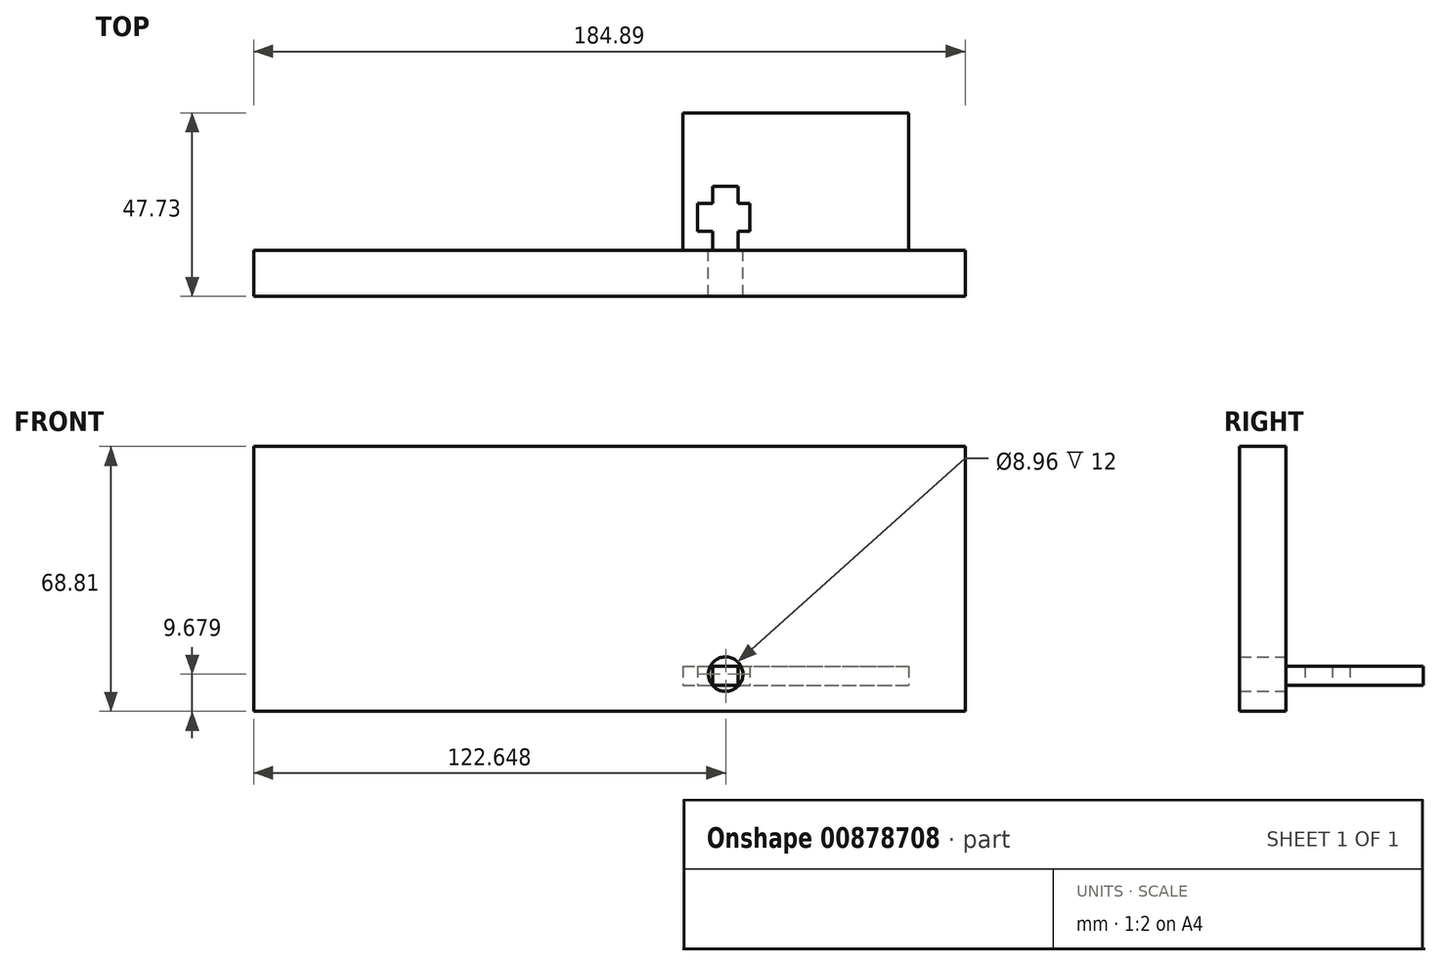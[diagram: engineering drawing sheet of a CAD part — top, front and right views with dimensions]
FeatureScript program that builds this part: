
annotation { "Feature Type Name" : "Feature", "Feature Type Description" : "" }
export const myFeature = defineFeature(function(context is Context, id is Id, definition is map)
    precondition{}
    {
        {
            var Q0;
            Q0=qCreatedBy(makeId("Top.planeOp"),FACE);
            var sketch = newSketch(context, id + "F0", { "sketchPlane" : qUnion([Q0])});
            skLineSegment(sketch, "E0.bottom", {"start": v(0, 0) * mm, "end": v(58.66, 0) * mm});
            skLineSegment(sketch, "E0.top", {"start": v(0, 35.73) * mm, "end": v(58.66, 35.73) * mm});
            skLineSegment(sketch, "E0.left", {"start": v(0, 0) * mm, "end": v(0, 35.73) * mm});
            skLineSegment(sketch, "E0.right", {"start": v(58.66, 0) * mm, "end": v(58.66, 35.73) * mm});
            skLineSegment(sketch, "E1.bottom", {"start": v(7.74, 0) * mm, "end": v(14.43, 0) * mm});
            skLineSegment(sketch, "E1.top", {"start": v(7.74, 4.95) * mm, "end": v(14.43, 4.95) * mm});
            skLineSegment(sketch, "E1.left", {"start": v(7.74, 0) * mm, "end": v(7.74, 4.95) * mm});
            skLineSegment(sketch, "E1.right", {"start": v(14.43, 0) * mm, "end": v(14.43, 4.95) * mm});
            skLineSegment(sketch, "E2.bottom", {"start": v(3.84, 4.95) * mm, "end": v(17.45, 4.95) * mm});
            skLineSegment(sketch, "E2.top", {"start": v(3.84, 12.14) * mm, "end": v(17.45, 12.14) * mm});
            skLineSegment(sketch, "E2.left", {"start": v(3.84, 4.95) * mm, "end": v(3.84, 12.14) * mm});
            skLineSegment(sketch, "E2.right", {"start": v(17.45, 4.95) * mm, "end": v(17.45, 12.14) * mm});
            skPoint(sketch, "E3.firstSnap0", {"position": v(10.65, 12.14) * mm});
            skLineSegment(sketch, "E3.bottom", {"start": v(7.74, 12.14) * mm, "end": v(14.43, 12.14) * mm});
            skLineSegment(sketch, "E3.top", {"start": v(7.74, 16.67) * mm, "end": v(14.43, 16.67) * mm});
            skLineSegment(sketch, "E3.left", {"start": v(7.74, 12.14) * mm, "end": v(7.74, 16.67) * mm});
            skLineSegment(sketch, "E3.right", {"start": v(14.43, 12.14) * mm, "end": v(14.43, 16.67) * mm});
            skSolve(sketch);
        }
        {
            var Q0;
            Q0=makeQuery(id+"F0.imprint","IMPRINT",FACE,{"disambiguationData":[TD([[makeQuery(id+"F0.imprint","IMPRINT",EDGE,{"derivedFrom":sQuery(id+"F0.wireOp",EDGE,"E0.top")}),-1.0]])]});
            extrude(context, id + "F1", {"entities" : qUnion([Q0]), "depth" : 5 * mm, "offsetDistance" : 25 * mm});
        }
        {
            var Q0;
            Q0=qCreatedBy(makeId("Front.planeOp"),FACE);
            var sketch = newSketch(context, id + "F2", { "sketchPlane" : qUnion([Q0])});
            skLineSegment(sketch, "E4.bottom", {"start": v(-111.52, 62.03) * mm, "end": v(73.37, 62.03) * mm});
            skLineSegment(sketch, "E4.top", {"start": v(-111.52, -6.78) * mm, "end": v(73.37, -6.78) * mm});
            skLineSegment(sketch, "E4.left", {"start": v(-111.52, 62.03) * mm, "end": v(-111.52, -6.78) * mm});
            skLineSegment(sketch, "E4.right", {"start": v(73.37, 62.03) * mm, "end": v(73.37, -6.78) * mm});
            skCircle(sketch, "E5", {"center": v(11.13, 2.9) * mm, "radius": 4.48 * mm});
            skSolve(sketch);
        }
        {
            var Q0;
            Q0=makeQuery(id+"F2.imprint","IMPRINT",FACE,{"disambiguationData":[TD([[makeQuery(id+"F2.imprint","IMPRINT",EDGE,{"derivedFrom":sQuery(id+"F2.wireOp",EDGE,"E4.bottom")}),-1.0]])]});
            extrude(context, id + "F3", {"entities" : qUnion([Q0]), "operationType" : NewBodyOperationType.ADD, "depth" : 12 * mm, "offsetDistance" : 25 * mm});
        }
    });
